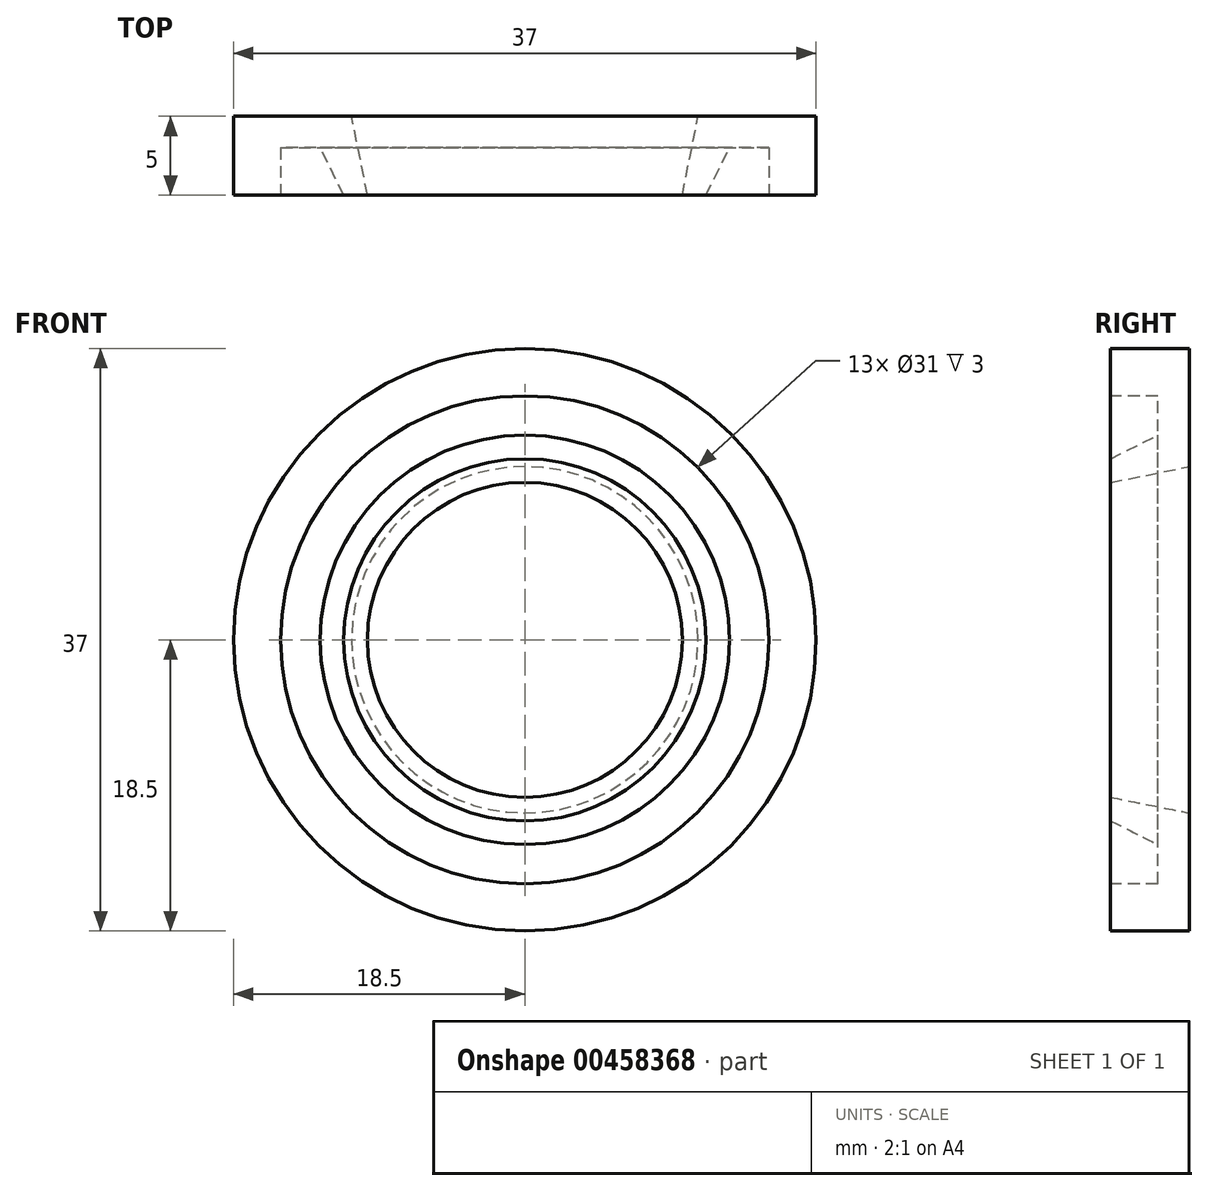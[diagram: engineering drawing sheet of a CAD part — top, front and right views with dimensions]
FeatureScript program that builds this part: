
annotation { "Feature Type Name" : "Feature", "Feature Type Description" : "" }
export const myFeature = defineFeature(function(context is Context, id is Id, definition is map)
    precondition{}
    {
        {
            var Q0;
            Q0=qCreatedBy(makeId("Right.planeOp"),FACE);
            var sketch = newSketch(context, id + "F0", { "sketchPlane" : qUnion([Q0])});
            skLineSegment(sketch, "E0", {"start": v(0, 11) * mm, "end": v(0, 18.5) * mm});
            skLineSegment(sketch, "E1", {"start": v(0, 18.5) * mm, "end": v(-5, 18.5) * mm});
            skLineSegment(sketch, "E2", {"start": v(-5, 18.5) * mm, "end": v(-5, 15.5) * mm});
            skLineSegment(sketch, "E3", {"start": v(-5, 15.5) * mm, "end": v(-2, 15.5) * mm});
            skLineSegment(sketch, "E4", {"start": v(-2, 15.5) * mm, "end": v(-2, 13) * mm});
            skLineSegment(sketch, "E5", {"start": v(-5, 11.5) * mm, "end": v(-5, 10) * mm, "construction": true});
            skLineSegment(sketch, "E6", {"start": v(-5, 11.5) * mm, "end": v(-5, 10) * mm});
            skLineSegment(sketch, "E7", {"start": v(-5, 11.5) * mm, "end": v(-2, 13) * mm});
            skLineSegment(sketch, "E8", {"start": v(0, 11) * mm, "end": v(-5, 10) * mm});
            skLineSegment(sketch, "E9", {"start": v(-8.08, 0) * mm, "end": v(16.53, 0) * mm, "construction": true});
            skSolve(sketch);
        }
        {
            var Q0;
            Q0=makeQuery(id+"F0.imprint","IMPRINT",FACE,{"disambiguationData":[TD([[makeQuery(id+"F0.imprint","IMPRINT",EDGE,{"derivedFrom":sQuery(id+"F0.wireOp",EDGE,"E0")}),1.0]])]});
            var Q1;
            Q1=sQuery(id+"F0.wireOp",EDGE,"E9");
            revolve(context, id + "F1", {"entities" : qUnion([Q0]), "axis" : qUnion([Q1]), "revolveType" : RevolveType.FULL});
        }
    });
